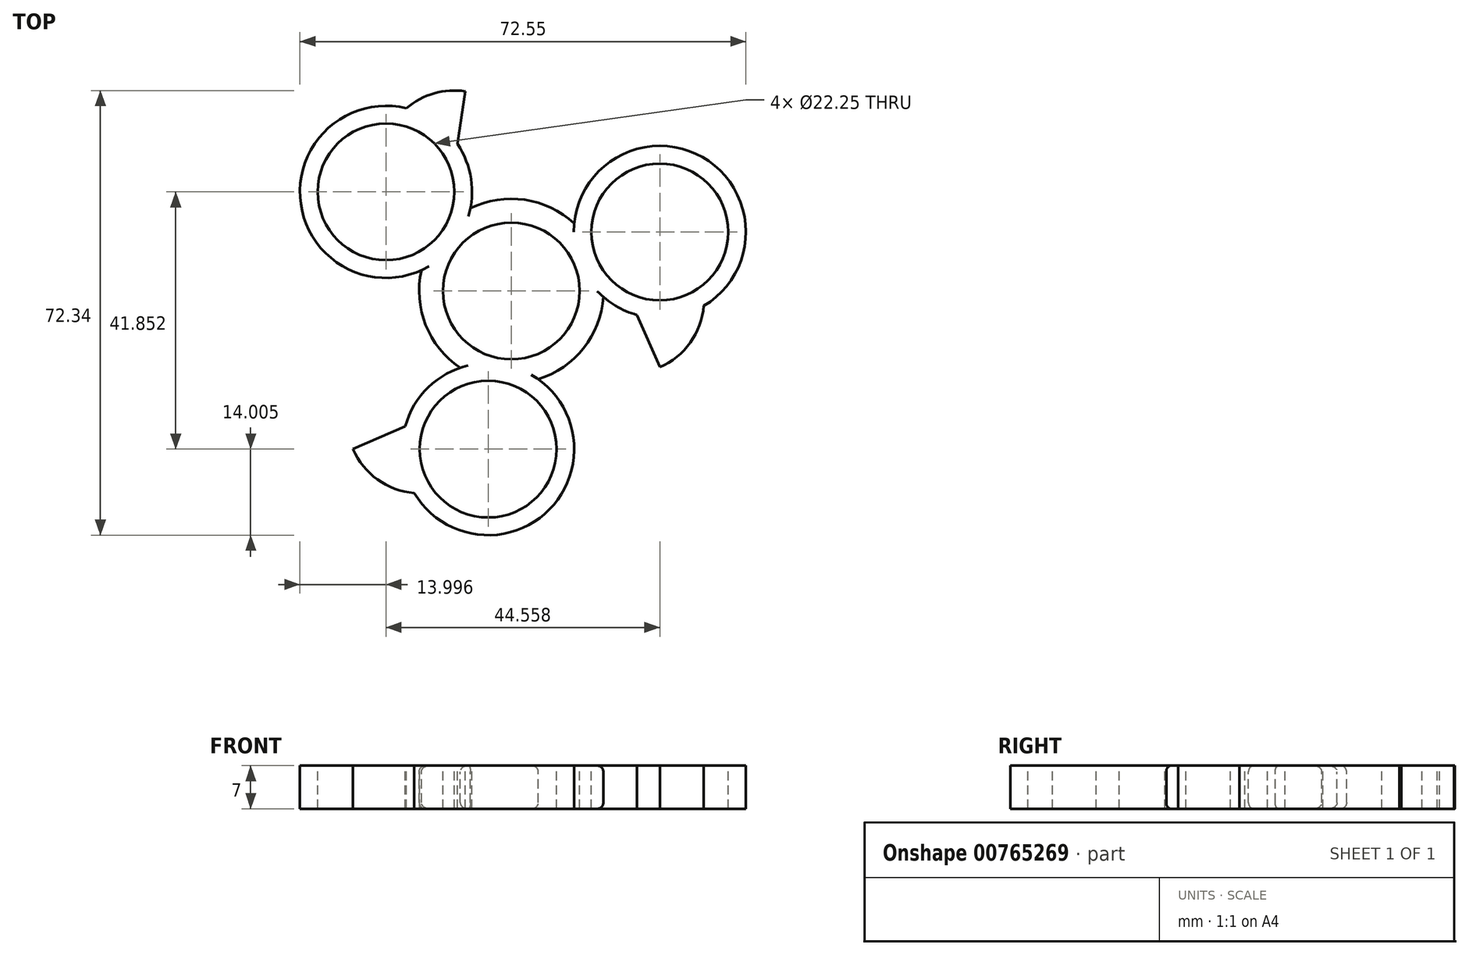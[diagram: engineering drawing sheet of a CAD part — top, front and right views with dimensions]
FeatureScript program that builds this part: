
annotation { "Feature Type Name" : "Feature", "Feature Type Description" : "" }
export const myFeature = defineFeature(function(context is Context, id is Id, definition is map)
    precondition{}
    {
        {
            var Q0;
            Q0=qCreatedBy(makeId("Top.planeOp"),FACE);
            var sketch = newSketch(context, id + "F0", { "sketchPlane" : qUnion([Q0])});
            skCircle(sketch, "E0", {"center": v(0, 0) * mm, "radius": 15 * mm});
            skCircle(sketch, "E1", {"center": v(0, 0) * mm, "radius": 11.12 * mm});
            skLineSegment(sketch, "E2", {"start": v(0, 0) * mm, "end": v(-20.4, 16.13) * mm});
            skLineSegment(sketch, "E3", {"start": v(0, 0) * mm, "end": v(-3.77, -25.73) * mm});
            skPoint(sketch, "E4.0.midPoint", {"position": v(-14.51, 11.47) * mm});
            skCircle(sketch, "E5", {"center": v(-3.77, -25.73) * mm, "radius": 14 * mm});
            skCircle(sketch, "E6", {"center": v(-20.4, 16.13) * mm, "radius": 14 * mm});
            skCircle(sketch, "E7", {"center": v(24.16, 9.6) * mm, "radius": 14 * mm});
            skCircle(sketch, "E8", {"center": v(-3.77, -25.73) * mm, "radius": 11.12 * mm});
            skLineSegment(sketch, "E9", {"start": v(0, 0) * mm, "end": v(24.16, 9.6) * mm});
            skCircle(sketch, "E10", {"center": v(24.16, 9.6) * mm, "radius": 11.12 * mm});
            skCircle(sketch, "E11", {"center": v(-20.4, 16.13) * mm, "radius": 11.12 * mm});
            skLineSegment(sketch, "E12", {"start": v(-20.4, 16.13) * mm, "end": v(-7.46, 32.48) * mm});
            skLineSegment(sketch, "E13", {"start": v(24.16, 9.6) * mm, "end": v(24.16, -12.4) * mm});
            skLineSegment(sketch, "E14", {"start": v(-3.77, -25.73) * mm, "end": v(-25.77, -25.73) * mm});
            skArc(sketch, "E15", {"start": v(-7.46, 32.48) * mm, "mid": v(-18.68, 28.06) * mm, "end": v(-20.4, 16.13) * mm});
            skArc(sketch, "E16", {"start": v(24.16, -12.4) * mm, "mid": v(31.37, -1.4) * mm, "end": v(24.16, 9.6) * mm});
            skArc(sketch, "E17", {"start": v(-25.77, -25.73) * mm, "mid": v(-14.77, -32.93) * mm, "end": v(-3.77, -25.73) * mm});
            skFitSpline(sketch, "E18", {"points": [v(-7.46, 32.48) * mm, v(-9.26, 20.61) * mm], "startDerivative": vector(-1.8, -11.86) * mm, "endDerivative": vector(-1.8, -11.86) * mm});
            skLineSegment(sketch, "E19", {"start": v(19.37, -1.4) * mm, "end": v(24.16, -12.4) * mm});
            skLineSegment(sketch, "E20", {"start": v(-25.77, -25.73) * mm, "end": v(-14.77, -20.93) * mm});
            skSolve(sketch);
        }
        {
            var Q0;
            {var subQ0=sQuery(id+"F0.wireOp",EDGE,"E16");var subQ1=sQuery(id+"F0.wireOp",EDGE,"E7");var subQ2=makeQuery(id+"F0.imprint","INTERSECT",VERTEX,{"derivedFrom":[subQ1,subQ0]});Q0=makeQuery(id+"F0.imprint","IMPRINT",FACE,{"disambiguationData":[TD([[makeQuery(id+"F0.imprint","IMPRINT",EDGE,{"disambiguationData":[TD([[subQ2,1.0]])],"derivedFrom":subQ1}),1.0]])]});}
            var Q1;
            {var subQ0=sQuery(id+"F0.wireOp",EDGE,"E16");var subQ1=sQuery(id+"F0.wireOp",EDGE,"E7");var subQ2=makeQuery(id+"F0.imprint","INTERSECT",VERTEX,{"derivedFrom":[subQ1,subQ0]});Q1=makeQuery(id+"F0.imprint","IMPRINT",FACE,{"disambiguationData":[TD([[makeQuery(id+"F0.imprint","IMPRINT",EDGE,{"disambiguationData":[TD([[subQ2,1.0]])],"derivedFrom":subQ1}),-1.0]])]});}
            var Q2;
            {var subQ0=sQuery(id+"F0.wireOp",EDGE,"E19");var subQ1=sQuery(id+"F0.wireOp",EDGE,"E7");var subQ2=makeQuery(id+"F0.imprint","INTERSECT",VERTEX,{"derivedFrom":[subQ1,subQ0]});Q2=makeQuery(id+"F0.imprint","IMPRINT",FACE,{"disambiguationData":[TD([[makeQuery(id+"F0.imprint","IMPRINT",EDGE,{"disambiguationData":[TD([[subQ2,-1.0]])],"derivedFrom":subQ1}),-1.0]])]});}
            var Q3;
            {var subQ0=sQuery(id+"F0.wireOp",EDGE,"E15");var subQ1=sQuery(id+"F0.wireOp",EDGE,"E6");var subQ2=makeQuery(id+"F0.imprint","INTERSECT",VERTEX,{"derivedFrom":[subQ1,subQ0]});Q3=makeQuery(id+"F0.imprint","IMPRINT",FACE,{"disambiguationData":[TD([[makeQuery(id+"F0.imprint","IMPRINT",EDGE,{"disambiguationData":[TD([[subQ2,1.0]])],"derivedFrom":subQ1}),-1.0]])]});}
            var Q4;
            {var subQ0=sQuery(id+"F0.wireOp",EDGE,"E18");var subQ1=sQuery(id+"F0.wireOp",EDGE,"E6");var subQ2=makeQuery(id+"F0.imprint","INTERSECT",VERTEX,{"derivedFrom":[subQ1,subQ0]});Q4=makeQuery(id+"F0.imprint","IMPRINT",FACE,{"disambiguationData":[TD([[makeQuery(id+"F0.imprint","IMPRINT",EDGE,{"disambiguationData":[TD([[subQ2,-1.0]])],"derivedFrom":subQ1}),-1.0]])]});}
            var Q5;
            {var subQ0=sQuery(id+"F0.wireOp",EDGE,"E20");var subQ1=sQuery(id+"F0.wireOp",EDGE,"E5");var subQ2=makeQuery(id+"F0.imprint","INTERSECT",VERTEX,{"derivedFrom":[subQ1,subQ0]});Q5=makeQuery(id+"F0.imprint","IMPRINT",FACE,{"disambiguationData":[TD([[makeQuery(id+"F0.imprint","IMPRINT",EDGE,{"disambiguationData":[TD([[subQ2,-1.0]])],"derivedFrom":subQ1}),-1.0]])]});}
            var Q6;
            {var subQ0=sQuery(id+"F0.wireOp",EDGE,"E17");var subQ1=sQuery(id+"F0.wireOp",EDGE,"E5");var subQ2=makeQuery(id+"F0.imprint","INTERSECT",VERTEX,{"derivedFrom":[subQ1,subQ0]});Q6=makeQuery(id+"F0.imprint","IMPRINT",FACE,{"disambiguationData":[TD([[makeQuery(id+"F0.imprint","IMPRINT",EDGE,{"disambiguationData":[TD([[subQ2,1.0]])],"derivedFrom":subQ1}),-1.0]])]});}
            var Q7;
            {var subQ1=sQuery(id+"F0.wireOp",EDGE,"E0");var subQ5=sQuery(id+"F0.wireOp",EDGE,"E6");var subQ7=makeQuery(id+"F0.imprint","INTERSECT",VERTEX,{"disambiguationData":[OD(0.0)],"derivedFrom":[subQ1,subQ5]});Q7=makeQuery(id+"F0.imprint","IMPRINT",FACE,{"disambiguationData":[TD([[makeQuery(id+"F0.imprint","IMPRINT",EDGE,{"disambiguationData":[TD([[subQ7,-1.0]])],"derivedFrom":subQ1}),-1.0]])]});}
            var Q8;
            {var subQ0=sQuery(id+"F0.wireOp",EDGE,"E7");var subQ1=sQuery(id+"F0.wireOp",EDGE,"E0");var subQ2=makeQuery(id+"F0.imprint","INTERSECT",VERTEX,{"disambiguationData":[OD(0.0)],"derivedFrom":[subQ1,subQ0]});Q8=makeQuery(id+"F0.imprint","IMPRINT",FACE,{"disambiguationData":[TD([[makeQuery(id+"F0.imprint","IMPRINT",EDGE,{"disambiguationData":[TD([[subQ2,1.0]])],"derivedFrom":subQ1}),-1.0]])]});}
            var Q9;
            {var subQ1=sQuery(id+"F0.wireOp",EDGE,"E0");var subQ5=sQuery(id+"F0.wireOp",EDGE,"E7");var subQ6=makeQuery(id+"F0.imprint","INTERSECT",VERTEX,{"disambiguationData":[OD(1.0)],"derivedFrom":[subQ1,subQ5]});Q9=makeQuery(id+"F0.imprint","IMPRINT",FACE,{"disambiguationData":[TD([[makeQuery(id+"F0.imprint","IMPRINT",EDGE,{"disambiguationData":[TD([[subQ6,-1.0]])],"derivedFrom":subQ1}),-1.0]])]});}
            var Q10;
            {var subQ0=sQuery(id+"F0.wireOp",EDGE,"E6");var subQ1=sQuery(id+"F0.wireOp",EDGE,"E0");var subQ2=makeQuery(id+"F0.imprint","INTERSECT",VERTEX,{"disambiguationData":[OD(1.0)],"derivedFrom":[subQ1,subQ0]});Q10=makeQuery(id+"F0.imprint","IMPRINT",FACE,{"disambiguationData":[TD([[makeQuery(id+"F0.imprint","IMPRINT",EDGE,{"disambiguationData":[TD([[subQ2,1.0]])],"derivedFrom":subQ1}),-1.0]])]});}
            var Q11;
            {var subQ0=sQuery(id+"F0.wireOp",EDGE,"E15");var subQ1=sQuery(id+"F0.wireOp",EDGE,"E6");var subQ2=makeQuery(id+"F0.imprint","INTERSECT",VERTEX,{"derivedFrom":[subQ1,subQ0]});Q11=makeQuery(id+"F0.imprint","IMPRINT",FACE,{"disambiguationData":[TD([[makeQuery(id+"F0.imprint","IMPRINT",EDGE,{"disambiguationData":[TD([[subQ2,1.0]])],"derivedFrom":subQ1}),1.0]])]});}
            var Q12;
            {var subQ1=sQuery(id+"F0.wireOp",EDGE,"E0");var subQ5=sQuery(id+"F0.wireOp",EDGE,"E5");var subQ8=makeQuery(id+"F0.imprint","INTERSECT",VERTEX,{"disambiguationData":[OD(0.0)],"derivedFrom":[subQ1,subQ5]});Q12=makeQuery(id+"F0.imprint","IMPRINT",FACE,{"disambiguationData":[TD([[makeQuery(id+"F0.imprint","IMPRINT",EDGE,{"disambiguationData":[TD([[subQ8,-1.0]])],"derivedFrom":subQ1}),-1.0]])]});}
            var Q13;
            {var subQ0=sQuery(id+"F0.wireOp",EDGE,"E5");var subQ1=sQuery(id+"F0.wireOp",EDGE,"E0");var subQ2=makeQuery(id+"F0.imprint","INTERSECT",VERTEX,{"disambiguationData":[OD(1.0)],"derivedFrom":[subQ1,subQ0]});Q13=makeQuery(id+"F0.imprint","IMPRINT",FACE,{"disambiguationData":[TD([[makeQuery(id+"F0.imprint","IMPRINT",EDGE,{"disambiguationData":[TD([[subQ2,1.0]])],"derivedFrom":subQ1}),-1.0]])]});}
            var Q14;
            {var subQ0=sQuery(id+"F0.wireOp",EDGE,"E17");var subQ1=sQuery(id+"F0.wireOp",EDGE,"E5");var subQ2=makeQuery(id+"F0.imprint","INTERSECT",VERTEX,{"derivedFrom":[subQ1,subQ0]});Q14=makeQuery(id+"F0.imprint","IMPRINT",FACE,{"disambiguationData":[TD([[makeQuery(id+"F0.imprint","IMPRINT",EDGE,{"disambiguationData":[TD([[subQ2,1.0]])],"derivedFrom":subQ1}),1.0]])]});}
            var Q15;
            {var subQ7=sQuery(id+"F0.wireOp",EDGE,"E7");var subQ9=sQuery(id+"F0.wireOp",EDGE,"E0");var subQ11=makeQuery(id+"F0.imprint","INTERSECT",VERTEX,{"disambiguationData":[OD(0.0)],"derivedFrom":[subQ9,subQ7]});Q15=makeQuery(id+"F0.imprint","IMPRINT",FACE,{"disambiguationData":[TD([[makeQuery(id+"F0.imprint","IMPRINT",EDGE,{"disambiguationData":[TD([[subQ11,-1.0]])],"derivedFrom":subQ9}),1.0]])]});}
            var Q16;
            {var subQ3=sQuery(id+"F0.wireOp",EDGE,"E5");var subQ5=sQuery(id+"F0.wireOp",EDGE,"E0");var subQ6=makeQuery(id+"F0.imprint","INTERSECT",VERTEX,{"disambiguationData":[OD(1.0)],"derivedFrom":[subQ5,subQ3]});Q16=makeQuery(id+"F0.imprint","IMPRINT",FACE,{"disambiguationData":[TD([[makeQuery(id+"F0.imprint","IMPRINT",EDGE,{"disambiguationData":[TD([[subQ6,-1.0]])],"derivedFrom":subQ5}),1.0]])]});}
            var Q17;
            {var subQ0=sQuery(id+"F0.wireOp",EDGE,"E7");var subQ1=sQuery(id+"F0.wireOp",EDGE,"E0");var subQ2=makeQuery(id+"F0.imprint","INTERSECT",VERTEX,{"disambiguationData":[OD(1.0)],"derivedFrom":[subQ1,subQ0]});Q17=makeQuery(id+"F0.imprint","IMPRINT",FACE,{"disambiguationData":[TD([[makeQuery(id+"F0.imprint","IMPRINT",EDGE,{"disambiguationData":[TD([[subQ2,-1.0]])],"derivedFrom":subQ1}),1.0]])]});}
            var Q18;
            {var subQ0=sQuery(id+"F0.wireOp",EDGE,"E7");var subQ1=sQuery(id+"F0.wireOp",EDGE,"E0");var subQ2=makeQuery(id+"F0.imprint","INTERSECT",VERTEX,{"disambiguationData":[OD(0.0)],"derivedFrom":[subQ1,subQ0]});Q18=makeQuery(id+"F0.imprint","IMPRINT",FACE,{"disambiguationData":[TD([[makeQuery(id+"F0.imprint","IMPRINT",EDGE,{"disambiguationData":[TD([[subQ2,1.0]])],"derivedFrom":subQ1}),1.0]])]});}
            var Q19;
            {var subQ7=sQuery(id+"F0.wireOp",EDGE,"E6");var subQ9=sQuery(id+"F0.wireOp",EDGE,"E0");var subQ10=makeQuery(id+"F0.imprint","INTERSECT",VERTEX,{"disambiguationData":[OD(1.0)],"derivedFrom":[subQ9,subQ7]});Q19=makeQuery(id+"F0.imprint","IMPRINT",FACE,{"disambiguationData":[TD([[makeQuery(id+"F0.imprint","IMPRINT",EDGE,{"disambiguationData":[TD([[subQ10,-1.0]])],"derivedFrom":subQ9}),1.0]])]});}
            var Q20;
            {var subQ0=sQuery(id+"F0.wireOp",EDGE,"E6");var subQ1=sQuery(id+"F0.wireOp",EDGE,"E0");var subQ2=makeQuery(id+"F0.imprint","INTERSECT",VERTEX,{"disambiguationData":[OD(1.0)],"derivedFrom":[subQ1,subQ0]});Q20=makeQuery(id+"F0.imprint","IMPRINT",FACE,{"disambiguationData":[TD([[makeQuery(id+"F0.imprint","IMPRINT",EDGE,{"disambiguationData":[TD([[subQ2,1.0]])],"derivedFrom":subQ1}),1.0]])]});}
            var Q21;
            {var subQ0=sQuery(id+"F0.wireOp",EDGE,"E5");var subQ1=sQuery(id+"F0.wireOp",EDGE,"E0");var subQ2=makeQuery(id+"F0.imprint","INTERSECT",VERTEX,{"disambiguationData":[OD(0.0)],"derivedFrom":[subQ1,subQ0]});Q21=makeQuery(id+"F0.imprint","IMPRINT",FACE,{"disambiguationData":[TD([[makeQuery(id+"F0.imprint","IMPRINT",EDGE,{"disambiguationData":[TD([[subQ2,-1.0]])],"derivedFrom":subQ1}),1.0]])]});}
            var Q22;
            {var subQ0=sQuery(id+"F0.wireOp",EDGE,"E5");var subQ1=sQuery(id+"F0.wireOp",EDGE,"E0");var subQ2=makeQuery(id+"F0.imprint","INTERSECT",VERTEX,{"disambiguationData":[OD(1.0)],"derivedFrom":[subQ1,subQ0]});Q22=makeQuery(id+"F0.imprint","IMPRINT",FACE,{"disambiguationData":[TD([[makeQuery(id+"F0.imprint","IMPRINT",EDGE,{"disambiguationData":[TD([[subQ2,1.0]])],"derivedFrom":subQ1}),1.0]])]});}
            var Q23;
            {var subQ0=sQuery(id+"F0.wireOp",EDGE,"E6");var subQ1=sQuery(id+"F0.wireOp",EDGE,"E0");var subQ2=makeQuery(id+"F0.imprint","INTERSECT",VERTEX,{"disambiguationData":[OD(0.0)],"derivedFrom":[subQ1,subQ0]});Q23=makeQuery(id+"F0.imprint","IMPRINT",FACE,{"disambiguationData":[TD([[makeQuery(id+"F0.imprint","IMPRINT",EDGE,{"disambiguationData":[TD([[subQ2,-1.0]])],"derivedFrom":subQ1}),1.0]])]});}
            extrude(context, id + "F1", {"entities" : qUnion([Q0, Q1, Q2, Q3, Q4, Q5, Q6, Q7, Q8, Q9, Q10, Q11, Q12, Q13, Q14, Q15, Q16, Q17, Q18, Q19, Q20, Q21, Q22, Q23]), "oppositeDirection" : true, "depth" : 7 * mm, "offsetDistance" : 25 * mm});
        }
        {
            var Q0;
            {var subQ0=sQuery(id+"F0.wireOp",EDGE,"E0");Q0=makeQuery(id+"F1.opExtrude","CAP_EDGE",EDGE,{"disambiguationData":[OSD([subQ0]),TDD([makeQuery(id+"F0.imprint","IMPRINT",EDGE,{"disambiguationData":[TD([[makeQuery(id+"F0.imprint","INTERSECT",VERTEX,{"disambiguationData":[OD(1.0)],"derivedFrom":[subQ0,sQuery(id+"F0.wireOp",EDGE,"E6")]}),-1.0]])],"derivedFrom":subQ0})])],"isStart":false});}
            var Q1;
            {var subQ0=sQuery(id+"F0.wireOp",EDGE,"E0");Q1=makeQuery(id+"F1.opExtrude","CAP_EDGE",EDGE,{"disambiguationData":[OSD([subQ0]),TDD([makeQuery(id+"F0.imprint","IMPRINT",EDGE,{"disambiguationData":[TD([[makeQuery(id+"F0.imprint","INTERSECT",VERTEX,{"disambiguationData":[OD(1.0)],"derivedFrom":[subQ0,sQuery(id+"F0.wireOp",EDGE,"E6")]}),-1.0]])],"derivedFrom":subQ0})])],"isStart":true});}
            var Q2;
            {var subQ0=sQuery(id+"F0.wireOp",EDGE,"E0");Q2=makeQuery(id+"F1.opExtrude","CAP_EDGE",EDGE,{"disambiguationData":[OSD([subQ0]),TDD([makeQuery(id+"F0.imprint","IMPRINT",EDGE,{"disambiguationData":[TD([[makeQuery(id+"F0.imprint","INTERSECT",VERTEX,{"disambiguationData":[OD(1.0)],"derivedFrom":[subQ0,sQuery(id+"F0.wireOp",EDGE,"E5")]}),-1.0]])],"derivedFrom":subQ0})])],"isStart":false});}
            var Q3;
            {var subQ0=sQuery(id+"F0.wireOp",EDGE,"E0");Q3=makeQuery(id+"F1.opExtrude","CAP_EDGE",EDGE,{"disambiguationData":[OSD([subQ0]),TDD([makeQuery(id+"F0.imprint","IMPRINT",EDGE,{"disambiguationData":[TD([[makeQuery(id+"F0.imprint","INTERSECT",VERTEX,{"disambiguationData":[OD(1.0)],"derivedFrom":[subQ0,sQuery(id+"F0.wireOp",EDGE,"E5")]}),-1.0]])],"derivedFrom":subQ0})])],"isStart":true});}
            var Q4;
            {var subQ0=sQuery(id+"F0.wireOp",EDGE,"E0");Q4=makeQuery(id+"F1.opExtrude","CAP_EDGE",EDGE,{"disambiguationData":[OSD([subQ0]),TDD([makeQuery(id+"F0.imprint","IMPRINT",EDGE,{"disambiguationData":[TD([[makeQuery(id+"F0.imprint","INTERSECT",VERTEX,{"disambiguationData":[OD(0.0)],"derivedFrom":[subQ0,sQuery(id+"F0.wireOp",EDGE,"E7")]}),-1.0]])],"derivedFrom":subQ0})])],"isStart":true});}
            var Q5;
            {var subQ0=sQuery(id+"F0.wireOp",EDGE,"E0");Q5=makeQuery(id+"F1.opExtrude","CAP_EDGE",EDGE,{"disambiguationData":[OSD([subQ0]),TDD([makeQuery(id+"F0.imprint","IMPRINT",EDGE,{"disambiguationData":[TD([[makeQuery(id+"F0.imprint","INTERSECT",VERTEX,{"disambiguationData":[OD(0.0)],"derivedFrom":[subQ0,sQuery(id+"F0.wireOp",EDGE,"E7")]}),-1.0]])],"derivedFrom":subQ0})])],"isStart":false});}
            fillet(context, id + "F2", {"entities" : qUnion([Q0, Q1, Q2, Q3, Q4, Q5]), "radius" : 1 * mm, "tangentPropagation" : true, "allowEdgeOverflow" : false});
        }
    });
